# Revit family: 0068128
name_source: partatom
category: Lighting Fixtures
revit_build: Autodesk Revit 2017 (Build: 20160225_1515(x64)
units: mm (PartAtom-declared; Revit-internal decimal feet)

## family parameters
Cut with Voids When Loaded = No
Host = Face
Light Source = Yes
OmniClass Number = 23.80.70.00
OmniClass Title = Lighting
Part Type = Normal
Room Calculation Point = No
Round Connector Dimension = Use Diameter
Shared = No

## types (4) — shared parameters
Apparent Load = 24 VA
Assembly Code = D5020200
AssetType = Fixed
ClassificationName = Uniclass2015
ClassificationValue = EF_70_80
Color Filter = 16777215
Default Elevation = 1219 mm
Description = 5 metre IP65 LED reel with pre-attached 3M adhesive type;  equipped with 300 LEDs; 2750lm per 5m (550lm per 1m); 24V; 4000K; CRI80; SDCM <3; 50000 hrs (L70)
Dimming Lamp Color Temperature Shift = <None>
DocumentationLiterature = http://www.sylvania-lighting.com
ElectricShockClassification = Class III
Emit Shape Visible in Rendering = No
Emit from Rectangle Width = 12 mm  [stored 0.0393701 ft]
EmitSurfaceHeight_SYL = 4 mm  [stored 0.0131234 ft]
EmitSurfaceOffset_SYL = 1 mm  [stored 0.00328084 ft]
EndCapHeight_SYL = 6 mm  [stored 0.019685 ft]
EndCapLength_SYL = 10 mm  [stored 0.0328084 ft]
EndCapWidth_SYL = 14 mm  [stored 0.0459318 ft]
HeightWithSealing_SYL = 4 mm  [stored 0.0131234 ft]
IP20HO_SYL = No
IP20RGBW_SYL = No
IP20RGB_SYL = No
IP65HO_SYL = No
IP65_SYL = Yes
IP67RGBW_SYL = No
IP67RGB_SYL = No
IP67_SYL = No
IfcExportAs = IfcLightFixtureType
IfcExportType = IfcLightFixtureType
ImpactProtectionIndex = IK00
IngressProtection = IP65
InputVoltage = 24V DC
Keynote = 16500
Lamp = LED
LampColourRenderingIndex = 80
LampColourTemperature = 4000 K
LampMacAdamStep = 3
LampNominalLuminous = 2750 lm
LampsType = LED
LuminousEfficacy = 115 lm/W
Manufacturer = Feilo Sylvania
ManufacturerName = Feilo Sylvania
Material = other housing, silicone diffuser
Material_1_SYL = Aluminum
Material_2_SYL = LED
Material_3_SYL = ABS Plastic
Material_4_SYL = Polycarbonate, Clear
ModelNumber = 0068128
NominalDepth = 10 mm  [stored 0.0328084 ft]
NominalHeight = 4 mm  [stored 0.0131234 ft]
NominalLength = 5000 mm
Photometric Web File = 0068128.ies
PowerConsumption = 24 W
SealingVisibility_SYL = Yes
StartCapHeight_SYL = 6 mm  [stored 0.019685 ft]
StartCapLength_SYL = 10 mm  [stored 0.0328084 ft]
StartCapWidth_SYL = 14 mm  [stored 0.0459318 ft]
Tilt Angle = -90.00°
Type Image = <None>
URL = http://www.sylvania-lighting.com
Voltage = 24 V
Weight = 2.0 kg
Width_SYL = 12 mm  [stored 0.0393701 ft]
zero-valued in all types: Cost, PowerFactor

## per-type parameters (varying)
| type | Emit from Rectangle Length | Length_SYL | Model | ModelReference | Name | TypeName |
| 0068128 START FLEX IP65 840 2750LM - 500 mm | 498 mm  [stored 1.63386 ft] | 500 mm  [stored 1.64042 ft] | START Flex IP65 840 2750lm - 500 mm | START Flex IP65 840 2750lm - 500 mm | START Flex IP65 840 2750lm - 500 mm | START Flex IP65 840 2750lm - 500 mm |
| 0068128 START FLEX IP65 840 2750LM - 100 mm | 98 mm | 100 mm  [stored 0.328084 ft] | START Flex IP65 840 2750lm - 100 mm | START Flex IP65 840 2750lm - 100 mm | START Flex IP65 840 2750lm - 100 mm | START Flex IP65 840 2750lm - 100 mm |
| 0068128 START FLEX IP65 840 2750LM - 50 mm | 48 mm | 50 mm | START Flex IP65 840 2750lm - 50 mm | START Flex IP65 840 2750lm - 50 mm | START Flex IP65 840 2750lm - 50 mm | START Flex IP65 840 2750lm - 50 mm |
| 0068128 START FLEX IP65 840 2750LM - 10 mm | 8 mm  [stored 0.0262467 ft] | 10 mm  [stored 0.0328084 ft] | START Flex IP65 840 2750lm - 10 mm | START Flex IP65 840 2750lm - 10 mm | START Flex IP65 840 2750lm - 10 mm | START Flex IP65 840 2750lm - 10 mm |

note: [stored X ft] marks values corroborated as IEEE doubles in the binary element streams (Revit-internal decimal feet)

## geometry (parser evidence)
native form markers: Sweep x3
no freeform markers — native parametric forms only
